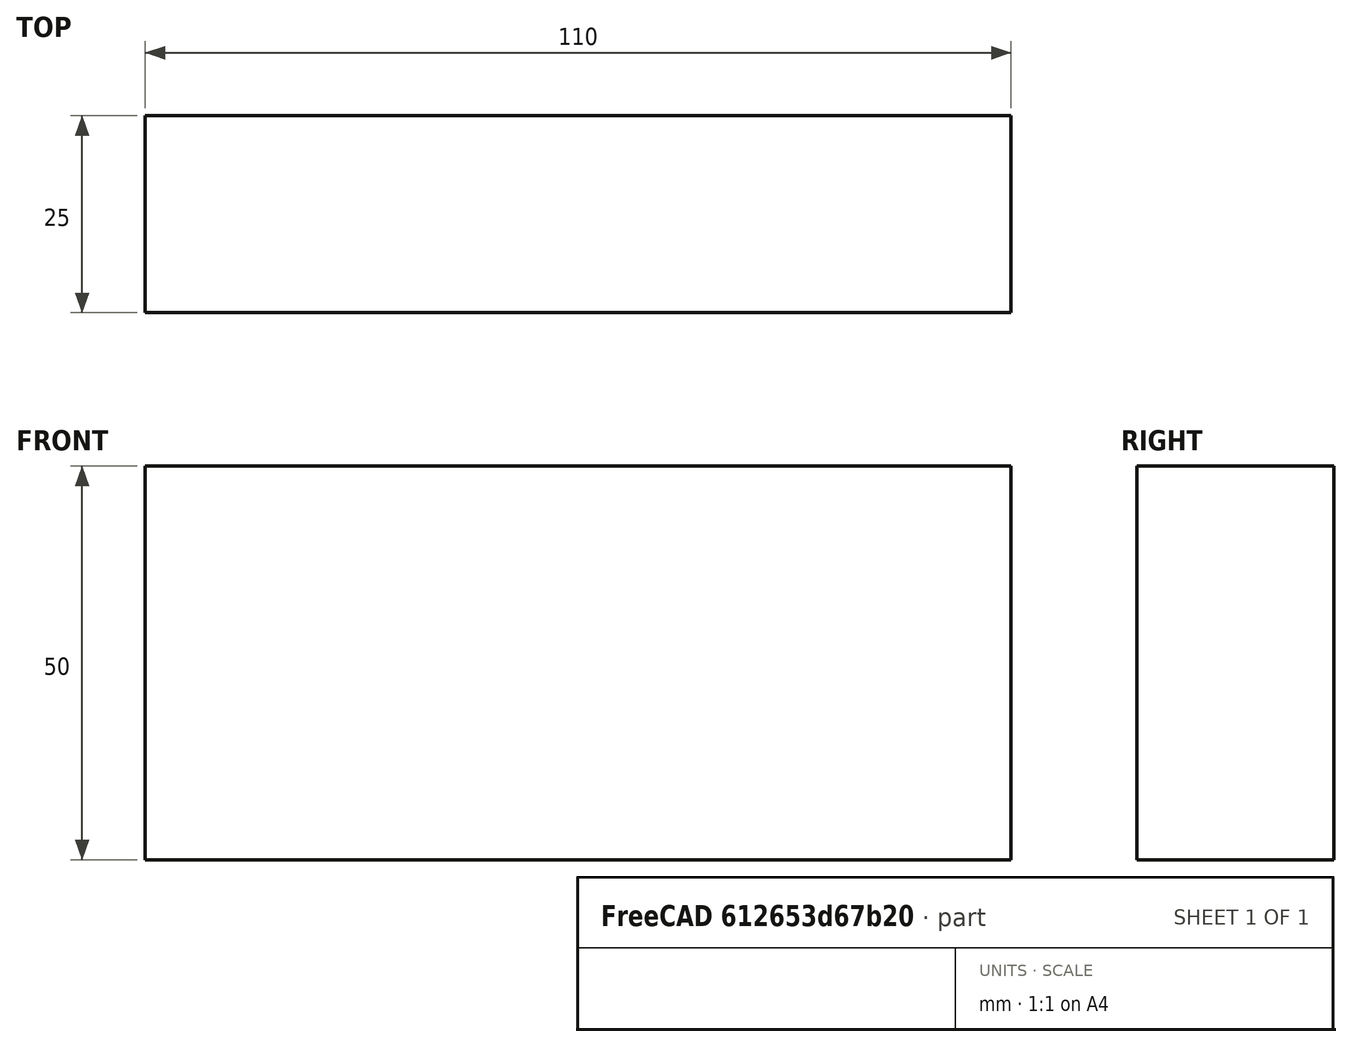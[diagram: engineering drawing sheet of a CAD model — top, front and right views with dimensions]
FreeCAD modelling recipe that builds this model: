
FCSTD DOCUMENT  (FreeCAD 0.15R4671 (Git))
Label: Flat Bar 110x25 EN10058 S235JR
License: All rights reserved
LicenseURL: http://en.wikipedia.org/wiki/All_rights_reserved
objects: Sketcher::SketchObject×1, Part::Extrusion×1
note: 2 computed .brp shape members not serialized (recipe doc carries the construction recipe); baked Part::Feature solids carry a one-line shape summary decoded from their .brp

FEATURE [Sketcher::SketchObject] Sketch
  sketch-geometry (4):
    g0: LineSegment StartX=-55 StartY=-12.5 StartZ=0 EndX=55 EndY=-12.5 EndZ=0
    g1: LineSegment StartX=55 StartY=-12.5 StartZ=0 EndX=55 EndY=12.5 EndZ=0
    g2: LineSegment StartX=55 StartY=12.5 StartZ=0 EndX=-55 EndY=12.5 EndZ=0
    g3: LineSegment StartX=-55 StartY=12.5 StartZ=0 EndX=-55 EndY=-12.5 EndZ=0
  constraints (12):
    c: Coincident(g0,g1)
    c: Coincident(g1,g2)
    c: Coincident(g2,g3)
    c: Coincident(g3,g0)
    c: Horizontal(g0)
    c: Horizontal(g2)
    c: Vertical(g1)
    c: Vertical(g3)
    c: Symmetric(g1,g2,g-2)
    c: Symmetric(g0,g1,g-1)
    c: DistanceY(g1) = 25
    c: DistanceX(g0) = 110
FEATURE [Part::Extrusion] Extrude  label="Flat Bar 110x25 EN10058 S235JR"
  Base = -> Sketch
  Dir = (0,0,50)
  Solid = true
